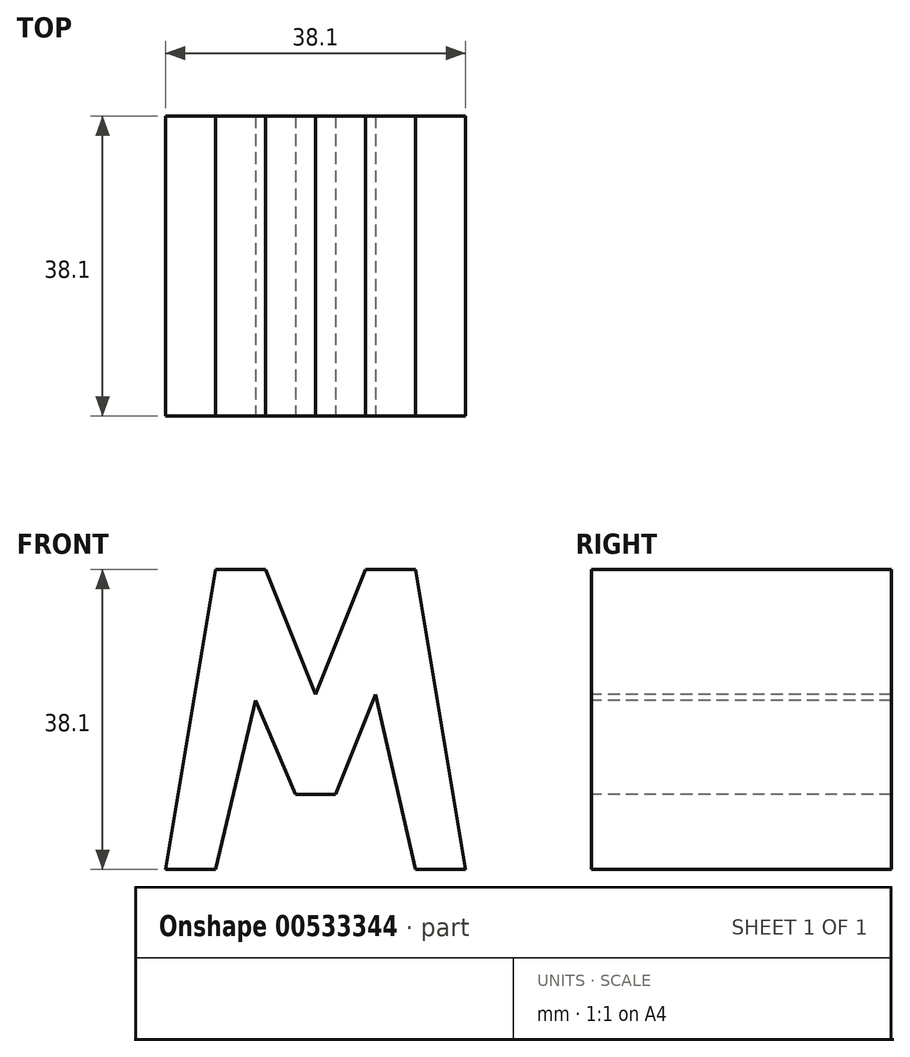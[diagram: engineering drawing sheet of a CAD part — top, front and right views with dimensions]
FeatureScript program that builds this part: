
annotation { "Feature Type Name" : "Feature", "Feature Type Description" : "" }
export const myFeature = defineFeature(function(context is Context, id is Id, definition is map)
    precondition{}
    {
        {
            var Q0;
            Q0=qCreatedBy(makeId("Front.planeOp"),FACE);
            var sketch = newSketch(context, id + "F0", { "sketchPlane" : qUnion([Q0])});
            skLineSegment(sketch, "E0", {"start": v(0, 0) * mm, "end": v(0, 38.1) * mm});
            skLineSegment(sketch, "E1", {"start": v(0, 38.1) * mm, "end": v(38.1, 38.1) * mm});
            skLineSegment(sketch, "E2", {"start": v(38.1, 38.1) * mm, "end": v(38.1, 0) * mm});
            skLineSegment(sketch, "E3", {"start": v(38.1, 0) * mm, "end": v(0, 0) * mm});
            skSolve(sketch);
        }
        {
            var Q0;
            Q0 = qSketchRegion(id + "F0", true);
            extrude(context, id + "F1", {"entities" : qUnion([Q0]), "depth" : 38.1 * mm, "offsetDistance" : 25.4 * mm});
        }
        {
            var Q0;
            Q0=qCreatedBy(makeId("Front.planeOp"),FACE);
            cPlane(context, id + "F2", {"entities" : qUnion([Q0]), "cplaneType" : CPlaneType.OFFSET, "offset" : 38.1 * mm, "width" : 152.4 * mm, "height" : 152.4 * mm});
        }
        {
            var Q0;
            Q0=qCreatedBy(makeId("Right.planeOp"),FACE);
            cPlane(context, id + "F3", {"entities" : qUnion([Q0]), "cplaneType" : CPlaneType.OFFSET, "offset" : 38.1 * mm, "width" : 152.4 * mm, "height" : 152.4 * mm});
        }
        {
            var Q0;
            Q0=qCreatedBy(id+"F2.planeOp",FACE);
            var sketch = newSketch(context, id + "F4", { "sketchPlane" : qUnion([Q0])});
            skLineSegment(sketch, "E4", {"start": v(0, 38.1) * mm, "end": v(0, 0) * mm});
            skLineSegment(sketch, "E5", {"start": v(0, 0) * mm, "end": v(38.1, 0) * mm});
            skLineSegment(sketch, "E6", {"start": v(38.1, 0) * mm, "end": v(38.1, 38.1) * mm});
            skLineSegment(sketch, "E7", {"start": v(38.1, 38.1) * mm, "end": v(0, 38.1) * mm});
            skLineSegment(sketch, "E8", {"start": v(6.35, 38.1) * mm, "end": v(0, 0) * mm});
            skLineSegment(sketch, "E9", {"start": v(6.35, 0) * mm, "end": v(11.43, 21.47) * mm});
            skLineSegment(sketch, "E10", {"start": v(11.43, 21.47) * mm, "end": v(16.51, 9.53) * mm});
            skLineSegment(sketch, "E11", {"start": v(16.51, 9.53) * mm, "end": v(21.6, 9.53) * mm});
            skLineSegment(sketch, "E12", {"start": v(21.6, 9.53) * mm, "end": v(26.67, 22.23) * mm});
            skLineSegment(sketch, "E13", {"start": v(26.67, 22.23) * mm, "end": v(31.75, 0) * mm});
            skLineSegment(sketch, "E14", {"start": v(38.1, 0) * mm, "end": v(31.75, 38.1) * mm});
            skLineSegment(sketch, "E15", {"start": v(25.4, 38.1) * mm, "end": v(19.05, 22.23) * mm});
            skLineSegment(sketch, "E16", {"start": v(19.05, 22.23) * mm, "end": v(12.7, 38.1) * mm});
            skSolve(sketch);
        }
        {
            var Q0;
            {var subQ0=sQuery(id+"F4.wireOp",EDGE,"E9");Q0=makeQuery(id+"F4.imprint","IMPRINT",FACE,{"disambiguationData":[TD([[makeQuery(id+"F4.imprint","IMPRINT",EDGE,{"derivedFrom":subQ0}),-1.0]])]});}
            var Q1;
            {var subQ0=sQuery(id+"F4.wireOp",EDGE,"E6");Q1=makeQuery(id+"F4.imprint","IMPRINT",FACE,{"disambiguationData":[TD([[makeQuery(id+"F4.imprint","IMPRINT",EDGE,{"derivedFrom":subQ0}),1.0]])]});}
            var Q2;
            {var subQ0=sQuery(id+"F4.wireOp",EDGE,"E15");Q2=makeQuery(id+"F4.imprint","IMPRINT",FACE,{"disambiguationData":[TD([[makeQuery(id+"F4.imprint","IMPRINT",EDGE,{"derivedFrom":subQ0}),-1.0]])]});}
            var Q3;
            {var subQ0=sQuery(id+"F4.wireOp",EDGE,"E4");Q3=makeQuery(id+"F4.imprint","IMPRINT",FACE,{"disambiguationData":[TD([[makeQuery(id+"F4.imprint","IMPRINT",EDGE,{"derivedFrom":subQ0}),1.0]])]});}
            extrude(context, id + "F5", {"entities" : qUnion([Q0, Q1, Q2, Q3]), "operationType" : NewBodyOperationType.REMOVE, "oppositeDirection" : true, "depth" : 38.1 * mm, "offsetDistance" : 25.4 * mm});
        }
    });
